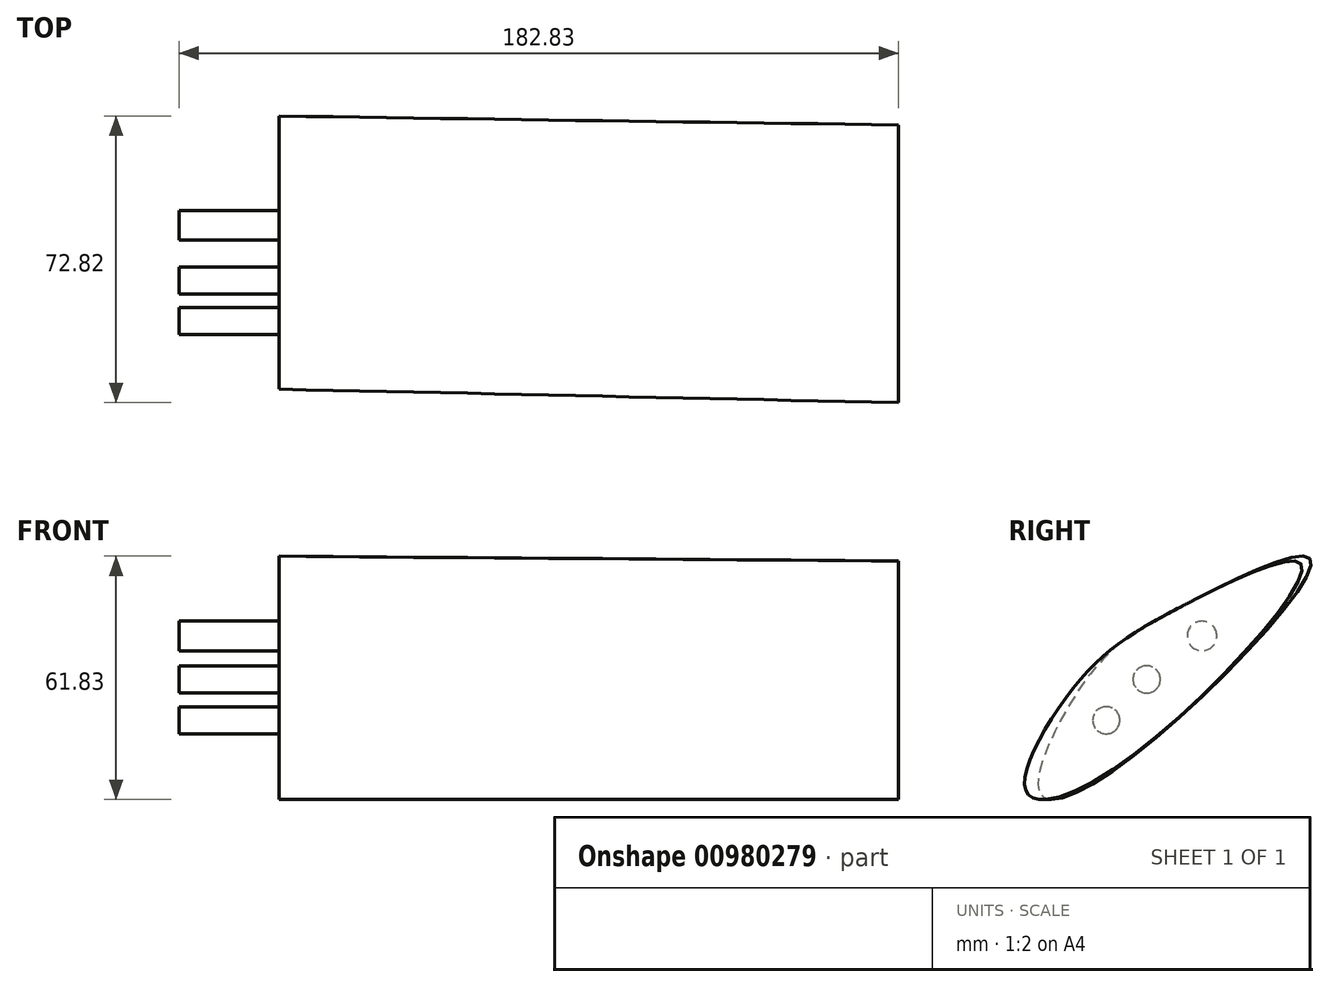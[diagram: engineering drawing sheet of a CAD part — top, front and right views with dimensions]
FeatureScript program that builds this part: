
annotation { "Feature Type Name" : "Feature", "Feature Type Description" : "" }
export const myFeature = defineFeature(function(context is Context, id is Id, definition is map)
    precondition{}
    {
        {
            var Q0;
            Q0=qCreatedBy(makeId("Right.planeOp"),FACE);
            var sketch = newSketch(context, id + "F0", { "sketchPlane" : qUnion([Q0])});
            skFitSpline(sketch, "E0", {"points": [v(0, 0) * mm, v(-24.16, -18.35) * mm, v(-36.28, -47.07) * mm, v(-16.72, -41.31) * mm, v(32.68, 11.8) * mm, v(0, 0) * mm]});
            skSolve(sketch);
        }
        {
            var Q0;
            Q0=qCreatedBy(makeId("Right.planeOp"),FACE);
            cPlane(context, id + "F1", {"entities" : qUnion([Q0]), "cplaneType" : CPlaneType.OFFSET, "offset" : 157.43 * mm, "width" : 152.4 * mm, "height" : 152.4 * mm});
        }
        {
            var Q0;
            Q0=qCreatedBy(id+"F1.planeOp",FACE);
            var sketch = newSketch(context, id + "F2", { "sketchPlane" : qUnion([Q0])});
            skFitSpline(sketch, "E1", {"points": [v(0, 0) * mm, v(-26.73, -19.74) * mm, v(-39.73, -46.64) * mm, v(-18.92, -42.37) * mm, v(30.43, 10.46) * mm, v(0, 0) * mm]});
            skSolve(sketch);
        }
        {
            var Q0;
            Q0=makeQuery(id+"F2.imprint","IMPRINT",FACE,{"disambiguationData":[TD([[makeQuery(id+"F2.imprint","IMPRINT",EDGE,{"derivedFrom":sQuery(id+"F2.wireOp",EDGE,"E1")}),1.0]])]});
            var Q1;
            Q1=makeQuery(id+"F0.imprint","IMPRINT",FACE,{"disambiguationData":[TD([[makeQuery(id+"F0.imprint","IMPRINT",EDGE,{"derivedFrom":sQuery(id+"F0.wireOp",EDGE,"E0")}),1.0]])]});
            loft(context, id + "F3", {"sheetProfilesArray" : [{ "sheetProfileEntities" : qUnion([Q0]) }, { "sheetProfileEntities" : qUnion([Q1]) }]});
        }
        {
            var Q0;
            Q0=makeQuery(id+"F3.opLoft","CAP_FACE",FACE,{"disambiguationData":[OSD([makeQuery(id+"F0.imprint","IMPRINT",FACE,{"disambiguationData":[TD([[makeQuery(id+"F0.imprint","IMPRINT",EDGE,{"derivedFrom":sQuery(id+"F0.wireOp",EDGE,"E0")}),1.0]])]})])],"isStart":true});
            var sketch = newSketch(context, id + "F4", { "sketchPlane" : qUnion([Q0])});
            skCircle(sketch, "E2", {"center": v(-5.1, -7.56) * mm, "radius": 3.76 * mm});
            skCircle(sketch, "E3", {"center": v(8.97, -18.59) * mm, "radius": 3.47 * mm});
            skCircle(sketch, "E4", {"center": v(19.24, -28.97) * mm, "radius": 3.44 * mm});
            skSolve(sketch);
        }
        {
            var Q0;
            Q0 = qSketchRegion(id + "F4", true);
            var Q1;
            Q1=makeQuery(id+"F4.imprint","IMPRINT",FACE,{"disambiguationData":[TD([[makeQuery(id+"F4.imprint","IMPRINT",EDGE,{"derivedFrom":sQuery(id+"F4.wireOp",EDGE,"E4")}),1.0]])]});
            extrude(context, id + "F5", {"entities" : qUnion([Q0, Q1]), "operationType" : NewBodyOperationType.ADD, "depth" : 25.4 * mm, "offsetDistance" : 25.4 * mm});
        }
    });
